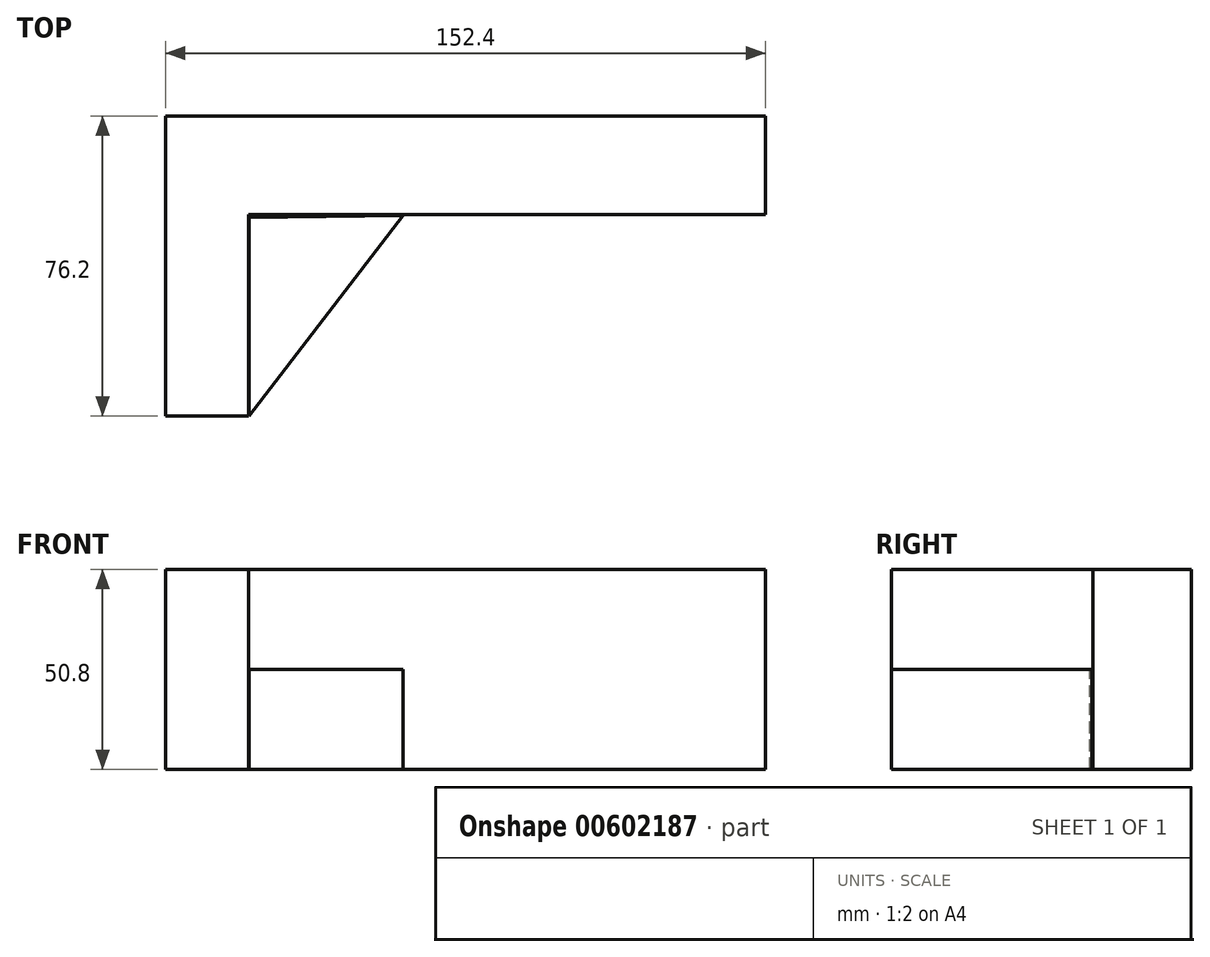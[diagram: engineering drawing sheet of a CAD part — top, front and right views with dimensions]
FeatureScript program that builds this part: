
annotation { "Feature Type Name" : "Feature", "Feature Type Description" : "" }
export const myFeature = defineFeature(function(context is Context, id is Id, definition is map)
    precondition{}
    {
        {
            var Q0;
            Q0=qCreatedBy(makeId("Front.planeOp"),FACE);
            var sketch = newSketch(context, id + "F0", { "sketchPlane" : qUnion([Q0])});
            skLineSegment(sketch, "E0.bottom", {"start": v(-77.57, 5.2) * mm, "end": v(74.83, 5.2) * mm});
            skLineSegment(sketch, "E0.top", {"start": v(-77.57, -45.6) * mm, "end": v(74.83, -45.6) * mm});
            skLineSegment(sketch, "E0.left", {"start": v(-77.57, 5.2) * mm, "end": v(-77.57, -45.6) * mm});
            skLineSegment(sketch, "E0.right", {"start": v(74.83, 5.2) * mm, "end": v(74.83, -45.6) * mm});
            skSolve(sketch);
        }
        {
            var Q0;
            Q0=makeQuery(id+"F0.imprint","IMPRINT",FACE,{"disambiguationData":[TD([[makeQuery(id+"F0.imprint","IMPRINT",EDGE,{"derivedFrom":sQuery(id+"F0.wireOp",EDGE,"E0.bottom")}),-1.0]])]});
            extrude(context, id + "F1", {"entities" : qUnion([Q0]), "oppositeDirection" : true, "depth" : 76.2 * mm, "offsetDistance" : 25.4 * mm});
        }
        {
            var Q0;
            Q0=makeQuery(id+"F1.opExtrude","SWEPT_FACE",FACE,{"disambiguationData":[OSD([sQuery(id+"F0.wireOp",EDGE,"E0.bottom")])]});
            var sketch = newSketch(context, id + "F2", { "sketchPlane" : qUnion([Q0])});
            skLineSegment(sketch, "E1", {"start": v(-56.44, 0) * mm, "end": v(-56.44, 51.18) * mm});
            skLineSegment(sketch, "E2", {"start": v(-56.44, 51.18) * mm, "end": v(74.83, 51.18) * mm});
            skSolve(sketch);
        }
        {
            var Q0;
            {var subQ0=sQuery(id+"F2.wireOp",EDGE,"E1");Q0=makeQuery(id+"F2.imprint","IMPRINT",FACE,{"disambiguationData":[TD([[makeQuery(id+"F2.imprint","IMPRINT",EDGE,{"derivedFrom":subQ0}),-1.0]])]});}
            extrude(context, id + "F3", {"entities" : qUnion([Q0]), "operationType" : NewBodyOperationType.REMOVE, "oppositeDirection" : true, "depth" : 50.8 * mm, "offsetDistance" : 25.4 * mm});
        }
        {
            var Q0;
            Q0=makeQuery(id+"F1.opExtrude","SWEPT_FACE",FACE,{"disambiguationData":[OSD([sQuery(id+"F0.wireOp",EDGE,"E0.bottom")])]});
            var sketch = newSketch(context, id + "F4", { "sketchPlane" : qUnion([Q0])});
            skSolve(sketch);
        }
        {
            var Q0;
            {var subQ0=sQuery(id+"F0.wireOp",EDGE,"E0.bottom");Q0=makeQuery(id+"F4.imprint","IMPRINT",FACE,{"disambiguationData":[TD([[makeQuery(id+"F4.imprint","IMPRINT",EDGE,{"derivedFrom":makeQuery(id+"F1.opExtrude","CAP_EDGE",EDGE,{"disambiguationData":[OSD([subQ0])],"isStart":false})}),-1.0]])]});}
            var sketch = newSketch(context, id + "F5", { "sketchPlane" : qUnion([Q0])});
            skLineSegment(sketch, "E3", {"start": v(-17.22, 50.95) * mm, "end": v(-56.42, 0) * mm});
            skLineSegment(sketch, "E4", {"start": v(-56.42, 0) * mm, "end": v(-56.42, 50.45) * mm});
            skLineSegment(sketch, "E5", {"start": v(-56.42, 50.45) * mm, "end": v(-17.22, 50.95) * mm});
            skSolve(sketch);
        }
        {
            var Q0;
            {var subQ0=sQuery(id+"F5.wireOp",EDGE,"E4");var subQ1=sQuery(id+"F5.wireOp",EDGE,"E3");var subQ2=makeQuery(id+"F5.imprint","INTERSECT",VERTEX,{"derivedFrom":[subQ1,subQ0]});Q0=makeQuery(id+"F5.imprint","IMPRINT",FACE,{"disambiguationData":[TD([[makeQuery(id+"F5.imprint","IMPRINT",EDGE,{"disambiguationData":[TD([[subQ2,1.0]])],"derivedFrom":subQ1}),-1.0]])]});}
            extrude(context, id + "F6", {"entities" : qUnion([Q0]), "operationType" : NewBodyOperationType.ADD, "oppositeDirection" : true, "depth" : 50.8 * mm, "offsetDistance" : 25.4 * mm});
        }
        {
            var Q0;
            Q0=makeQuery(id+"F6.opExtrude","CAP_FACE",FACE,{"disambiguationData":[OSD([sQuery(id+"F5.wireOp",EDGE,"E3"),sQuery(id+"F5.wireOp",EDGE,"E4"),sQuery(id+"F5.wireOp",EDGE,"E5")])],"isStart":true});
            extrude(context, id + "F7", {"entities" : qUnion([Q0]), "operationType" : NewBodyOperationType.REMOVE, "oppositeDirection" : true, "depth" : 25.4 * mm, "offsetDistance" : 25.4 * mm});
        }
    });
